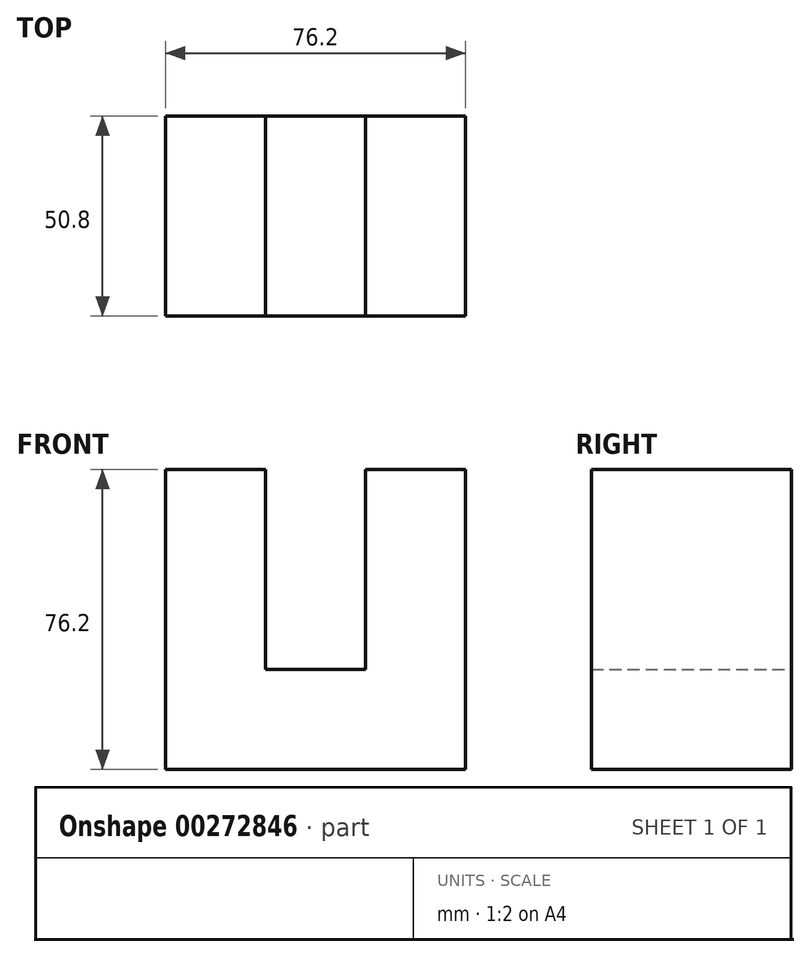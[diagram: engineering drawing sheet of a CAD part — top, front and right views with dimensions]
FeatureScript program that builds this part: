
annotation { "Feature Type Name" : "Feature", "Feature Type Description" : "" }
export const myFeature = defineFeature(function(context is Context, id is Id, definition is map)
    precondition{}
    {
        {
            var Q0;
            Q0=qCreatedBy(makeId("Front.planeOp"),FACE);
            var sketch = newSketch(context, id + "F0", { "sketchPlane" : qUnion([Q0])});
            skLineSegment(sketch, "E0.bottom", {"start": v(0, 0) * mm, "end": v(-76.2, 0) * mm});
            skLineSegment(sketch, "E0.top", {"start": v(0, 0) * mm, "end": v(-76.2, 0) * mm});
            skLineSegment(sketch, "E0.left", {"start": v(0, 0) * mm, "end": v(0, 0) * mm});
            skLineSegment(sketch, "E0.right", {"start": v(-76.2, 0) * mm, "end": v(-76.2, 0) * mm});
            skLineSegment(sketch, "E1.top", {"start": v(-76.2, 76.2) * mm, "end": v(-76.2, 76.2) * mm});
            skLineSegment(sketch, "E1.left", {"start": v(-76.2, 0) * mm, "end": v(-76.2, 76.2) * mm});
            skLineSegment(sketch, "E1.right", {"start": v(-76.2, 0) * mm, "end": v(-76.2, 76.2) * mm});
            skLineSegment(sketch, "E2", {"start": v(-76.2, 76.2) * mm, "end": v(-50.8, 76.2) * mm});
            skLineSegment(sketch, "E3", {"start": v(-50.8, 76.2) * mm, "end": v(-50.8, 25.4) * mm});
            skLineSegment(sketch, "E4", {"start": v(-50.8, 25.4) * mm, "end": v(-25.4, 25.4) * mm});
            skLineSegment(sketch, "E5", {"start": v(-25.4, 25.4) * mm, "end": v(-25.4, 76.2) * mm});
            skLineSegment(sketch, "E6", {"start": v(-25.4, 76.2) * mm, "end": v(0, 76.2) * mm});
            skLineSegment(sketch, "E7", {"start": v(0, 76.2) * mm, "end": v(0, 0) * mm});
            skSolve(sketch);
        }
        {
            var Q0;
            Q0 = qSketchRegion(id + "F0", true);
            extrude(context, id + "F1", {"entities" : qUnion([Q0]), "depth" : 50.8 * mm});
        }
    });
